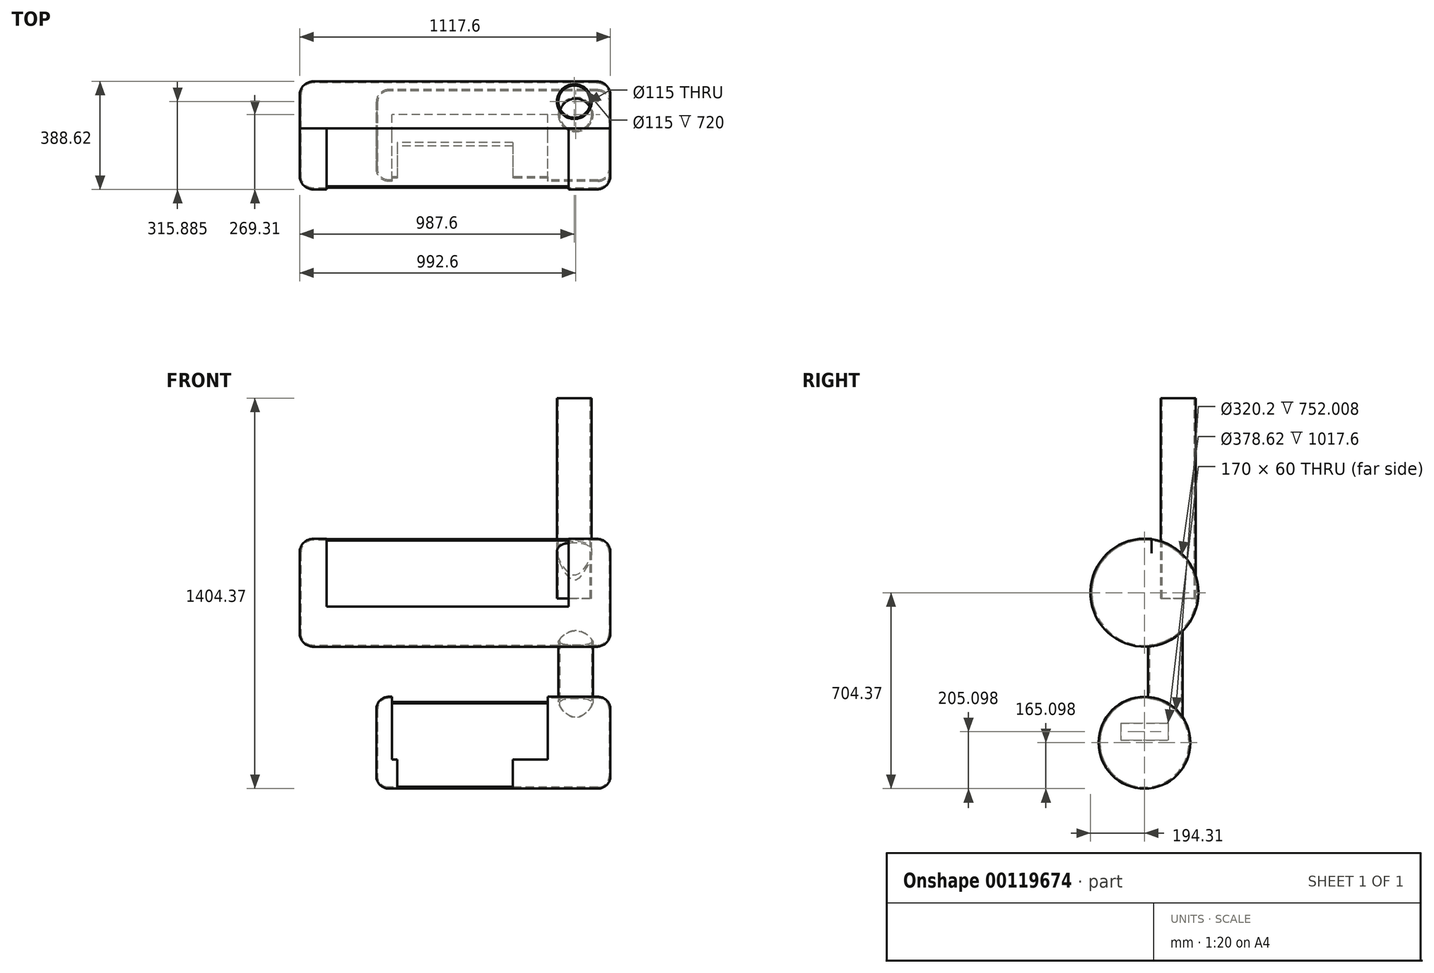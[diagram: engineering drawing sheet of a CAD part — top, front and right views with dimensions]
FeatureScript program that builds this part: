
annotation { "Feature Type Name" : "Feature", "Feature Type Description" : "" }
export const myFeature = defineFeature(function(context is Context, id is Id, definition is map)
    precondition{}
    {
        {
            var Q0;
            Q0=qCreatedBy(makeId("Front.planeOp"),FACE);
            var sketch = newSketch(context, id + "F0", { "sketchPlane" : qUnion([Q0])});
            skLineSegment(sketch, "E0", {"start": v(-542.74, 0) * mm, "end": v(519.1, 0) * mm, "construction": true});
            skLineSegment(sketch, "E1", {"start": v(-558.8, 0) * mm, "end": v(-558.8, 144.3) * mm});
            skLineSegment(sketch, "E2", {"start": v(-508.8, 194.31) * mm, "end": v(508.8, 194.31) * mm});
            skLineSegment(sketch, "E3", {"start": v(558.8, 144.31) * mm, "end": v(558.8, 0) * mm});
            skLineSegment(sketch, "E4", {"start": v(0, 0) * mm, "end": v(0, 194.3) * mm, "construction": true});
            skPoint(sketch, "E5.visualSharp", {"position": v(-558.8, 194.31) * mm});
            skArc(sketch, "E5.filletArc", {"start": v(-508.8, 194.3) * mm, "mid": v(-544.16, 179.67) * mm, "end": v(-558.8, 144.3) * mm});
            skPoint(sketch, "E6.visualSharp", {"position": v(558.8, 194.31) * mm});
            skArc(sketch, "E6.filletArc", {"start": v(558.8, 144.31) * mm, "mid": v(544.16, 179.67) * mm, "end": v(508.8, 194.31) * mm});
            skLineSegment(sketch, "E7.0", {"start": v(553.8, 144.31) * mm, "end": v(553.8, 0) * mm});
            skLineSegment(sketch, "E7.1", {"start": v(-508.8, 189.31) * mm, "end": v(508.8, 189.31) * mm});
            skLineSegment(sketch, "E7.2", {"start": v(-553.8, 0) * mm, "end": v(-553.8, 144.31) * mm});
            skPoint(sketch, "E8.visualSharp", {"position": v(-553.8, 189.31) * mm});
            skArc(sketch, "E8.filletArc", {"start": v(-508.8, 189.31) * mm, "mid": v(-540.62, 176.13) * mm, "end": v(-553.8, 144.31) * mm});
            skPoint(sketch, "E9.visualSharp", {"position": v(553.8, 189.31) * mm});
            skArc(sketch, "E9.filletArc", {"start": v(553.8, 144.31) * mm, "mid": v(540.62, 176.13) * mm, "end": v(508.8, 189.31) * mm});
            skLineSegment(sketch, "E10", {"start": v(-558.8, 0) * mm, "end": v(-553.8, 0) * mm});
            skLineSegment(sketch, "E11", {"start": v(553.8, 0) * mm, "end": v(558.8, 0) * mm});
            skSolve(sketch);
        }
        {
            var Q0;
            Q0 = qSketchRegion(id + "F0", true);
            extrude(context, id + "F1", {"entities" : qUnion([Q0]), "depth" : 25 * mm});
        }
        {
            var Q0;
            Q0=makeQuery(id+"F1.opExtrude","CAP_FACE",FACE,{"disambiguationData":[OSD([sQuery(id+"F0.wireOp",EDGE,"E1"),sQuery(id+"F0.wireOp",EDGE,"E2"),sQuery(id+"F0.wireOp",EDGE,"E3"),sQuery(id+"F0.wireOp",EDGE,"E5.filletArc"),sQuery(id+"F0.wireOp",EDGE,"E6.filletArc"),sQuery(id+"F0.wireOp",EDGE,"E7.0"),sQuery(id+"F0.wireOp",EDGE,"E7.1"),sQuery(id+"F0.wireOp",EDGE,"E7.2"),sQuery(id+"F0.wireOp",EDGE,"E8.filletArc"),sQuery(id+"F0.wireOp",EDGE,"E9.filletArc"),sQuery(id+"F0.wireOp",EDGE,"E10"),sQuery(id+"F0.wireOp",EDGE,"E11")])],"isStart":false});
            var Q1;
            Q1=makeQuery(id+"F1.opExtrude","CAP_EDGE",EDGE,{"disambiguationData":[OSD([sQuery(id+"F0.wireOp",EDGE,"E11")])],"isStart":false});
            revolve(context, id + "F2", {"operationType" : NewBodyOperationType.ADD, "entities" : qUnion([Q0]), "axis" : qUnion([Q1]), "revolveType" : RevolveType.FULL});
        }
        {
            var Q0;
            Q0=qCreatedBy(makeId("Front.planeOp"),FACE);
            cPlane(context, id + "F3", {"entities" : qUnion([Q0]), "cplaneType" : CPlaneType.OFFSET, "offset" : 25 * mm, "width" : 150 * mm, "height" : 150 * mm});
        }
        {
            var Q0;
            Q0=qCreatedBy(makeId("Front.planeOp"),FACE);
            var sketch = newSketch(context, id + "F4", { "sketchPlane" : qUnion([Q0])});
            skLineSegment(sketch, "E12", {"start": v(0, 125.35) * mm, "end": v(0, -125.48) * mm, "construction": true});
            skLineSegment(sketch, "E13.bottom", {"start": v(408.8, 526.72) * mm, "end": v(-461.2, 526.72) * mm});
            skLineSegment(sketch, "E13.top", {"start": v(408.8, -50) * mm, "end": v(-461.2, -50) * mm});
            skLineSegment(sketch, "E13.left", {"start": v(408.8, 526.72) * mm, "end": v(408.8, -50) * mm});
            skLineSegment(sketch, "E13.right", {"start": v(-461.2, 526.72) * mm, "end": v(-461.2, -50) * mm});
            skPoint(sketch, "E13.middle", {"position": v(-26.2, 238.36) * mm});
            skSolve(sketch);
        }
        {
            var Q0;
            Q0 = qSketchRegion(id + "F4", true);
            extrude(context, id + "F5", {"entities" : qUnion([Q0]), "operationType" : NewBodyOperationType.REMOVE, "endBound" : BoundingType.THROUGH_ALL, "depth" : 25 * mm});
        }
        {
            var Q0;
            Q0=qCreatedBy(id+"F3.planeOp",FACE);
            var sketch = newSketch(context, id + "F6", { "sketchPlane" : qUnion([Q0])});
            skLineSegment(sketch, "E14", {"start": v(0, 0) * mm, "end": v(0, -539.27) * mm, "construction": true});
            skLineSegment(sketch, "E15", {"start": v(-471.9, -539.27) * mm, "end": v(471.9, -539.27) * mm, "construction": true});
            skLineSegment(sketch, "E16", {"start": v(-283.2, -539.27) * mm, "end": v(-283.2, -419.17) * mm});
            skLineSegment(sketch, "E17", {"start": v(-238.2, -374.17) * mm, "end": v(513.8, -374.17) * mm});
            skLineSegment(sketch, "E18", {"start": v(558.8, -419.17) * mm, "end": v(558.8, -539.27) * mm});
            skPoint(sketch, "E19.visualSharp", {"position": v(558.8, -374.17) * mm});
            skArc(sketch, "E19.filletArc", {"start": v(558.8, -419.17) * mm, "mid": v(545.62, -387.35) * mm, "end": v(513.8, -374.17) * mm});
            skPoint(sketch, "E20.visualSharp", {"position": v(-283.2, -374.17) * mm});
            skArc(sketch, "E20.filletArc", {"start": v(-238.2, -374.17) * mm, "mid": v(-270.03, -387.35) * mm, "end": v(-283.2, -419.17) * mm});
            skLineSegment(sketch, "E21.0", {"start": v(553.8, -419.17) * mm, "end": v(553.8, -539.27) * mm});
            skLineSegment(sketch, "E21.1", {"start": v(-278.2, -539.27) * mm, "end": v(-278.2, -419.17) * mm});
            skArc(sketch, "E21.2", {"start": v(-238.2, -379.17) * mm, "mid": v(-266.5, -390.89) * mm, "end": v(-278.2, -419.17) * mm});
            skLineSegment(sketch, "E21.3", {"start": v(-238.2, -379.17) * mm, "end": v(513.8, -379.17) * mm});
            skArc(sketch, "E21.4", {"start": v(553.8, -419.17) * mm, "mid": v(542.08, -390.89) * mm, "end": v(513.8, -379.17) * mm});
            skLineSegment(sketch, "E22", {"start": v(-283.2, -539.27) * mm, "end": v(-278.2, -539.27) * mm});
            skLineSegment(sketch, "E23", {"start": v(553.8, -539.27) * mm, "end": v(558.8, -539.27) * mm});
            skSolve(sketch);
        }
        {
            var Q0;
            Q0 = qSketchRegion(id + "F6", true);
            var Q1;
            Q1=sQuery(id+"F6.wireOp",EDGE,"E23");
            revolve(context, id + "F7", {"entities" : qUnion([Q0]), "axis" : qUnion([Q1]), "revolveType" : RevolveType.FULL});
        }
        {
            var Q0;
            Q0=qCreatedBy(makeId("Top.planeOp"),FACE);
            cPlane(context, id + "F8", {"entities" : qUnion([Q0]), "cplaneType" : CPlaneType.OFFSET, "offset" : 300 * mm, "oppositeDirection" : true, "width" : 150 * mm, "height" : 150 * mm});
        }
        {
            var Q0;
            Q0=qCreatedBy(id+"F8.planeOp",FACE);
            var sketch = newSketch(context, id + "F9", { "sketchPlane" : qUnion([Q0])});
            skCircle(sketch, "E24", {"center": v(433.8, 50) * mm, "radius": 62.5 * mm});
            skCircle(sketch, "E25.0", {"center": v(433.8, 50) * mm, "radius": 57.5 * mm});
            skLineSegment(sketch, "E26", {"start": v(0, 0) * mm, "end": v(657.25, 0) * mm, "construction": true});
            skLineSegment(sketch, "E27", {"start": v(433.8, 50) * mm, "end": v(433.8, 0) * mm, "construction": true});
            skSolve(sketch);
        }
        {
            var Q0;
            Q0 = qSketchRegion(id + "F9", true);
            extrude(context, id + "F10", {"entities" : qUnion([Q0]), "operationType" : NewBodyOperationType.ADD, "endBound" : BoundingType.UP_TO_NEXT, "depth" : 25 * mm, "hasSecondDirection" : true, "secondDirectionBound" : SecondDirectionBoundingType.UP_TO_NEXT, "secondDirectionOppositeDirection" : true, "secondDirectionDepth" : 25 * mm});
        }
        {
            var Q0;
            Q0=qCreatedBy(makeId("Top.planeOp"),FACE);
            cPlane(context, id + "F11", {"entities" : qUnion([Q0]), "cplaneType" : CPlaneType.OFFSET, "offset" : 400 * mm, "oppositeDirection" : true, "width" : 150 * mm, "height" : 150 * mm});
        }
        {
            var Q0;
            Q0=qCreatedBy(id+"F11.planeOp",FACE);
            var sketch = newSketch(context, id + "F12", { "sketchPlane" : qUnion([Q0])});
            skLineSegment(sketch, "E28", {"start": v(0, 122.84) * mm, "end": v(0, -200) * mm, "construction": true});
            skLineSegment(sketch, "E29.bottom", {"start": v(-208.2, -50) * mm, "end": v(208.2, -50) * mm});
            skLineSegment(sketch, "E29.top", {"start": v(-208.2, -350) * mm, "end": v(208.2, -350) * mm});
            skLineSegment(sketch, "E29.left", {"start": v(-208.2, -50) * mm, "end": v(-208.2, -350) * mm});
            skLineSegment(sketch, "E29.right", {"start": v(208.2, -50) * mm, "end": v(208.2, -350) * mm});
            skPoint(sketch, "E29.middle", {"position": v(0, -200) * mm});
            skSolve(sketch);
        }
        {
            var Q0;
            Q0 = qSketchRegion(id + "F12", true);
            extrude(context, id + "F13", {"entities" : qUnion([Q0]), "operationType" : NewBodyOperationType.REMOVE, "oppositeDirection" : true, "depth" : 300 * mm, "hasSecondDirection" : true, "secondDirectionOppositeDirection" : false, "secondDirectionDepth" : 5.37 * mm});
        }
        {
            var Q0;
            Q0=qCreatedBy(makeId("Top.planeOp"),FACE);
            var sketch = newSketch(context, id + "F14", { "sketchPlane" : qUnion([Q0])});
            skCircle(sketch, "E30.0", {"center": v(433.8, 50) * mm, "radius": 62.5 * mm, "construction": true});
            skCircle(sketch, "E31", {"center": v(433.8, 50) * mm, "radius": 57.5 * mm});
            skSolve(sketch);
        }
        {
            var Q0;
            Q0 = qSketchRegion(id + "F14", true);
            extrude(context, id + "F15", {"entities" : qUnion([Q0]), "operationType" : NewBodyOperationType.REMOVE, "oppositeDirection" : true, "depth" : 600 * mm});
        }
        {
            var Q0;
            Q0=qCreatedBy(makeId("Front.planeOp"),FACE);
            cPlane(context, id + "F16", {"entities" : qUnion([Q0]), "cplaneType" : CPlaneType.OFFSET, "offset" : 300 * mm, "width" : 150 * mm, "height" : 150 * mm});
        }
        {
            var Q0;
            Q0=qCreatedBy(id+"F16.planeOp",FACE);
            var sketch = newSketch(context, id + "F17", { "sketchPlane" : qUnion([Q0])});
            skLineSegment(sketch, "E32.bottom", {"start": v(-226.2, -350) * mm, "end": v(333.8, -350) * mm});
            skLineSegment(sketch, "E32.top", {"start": v(-226.2, -600) * mm, "end": v(333.8, -600) * mm});
            skLineSegment(sketch, "E32.left", {"start": v(-226.2, -350) * mm, "end": v(-226.2, -600) * mm});
            skLineSegment(sketch, "E32.right", {"start": v(333.8, -350) * mm, "end": v(333.8, -600) * mm});
            skPoint(sketch, "E32.middle", {"position": v(53.8, -475) * mm});
            skSolve(sketch);
        }
        {
            var Q0;
            Q0 = qSketchRegion(id + "F17", true);
            extrude(context, id + "F18", {"entities" : qUnion([Q0]), "operationType" : NewBodyOperationType.REMOVE, "oppositeDirection" : true, "depth" : 350 * mm});
        }
        {
            var Q0;
            Q0=qCreatedBy(makeId("Top.planeOp"),FACE);
            cPlane(context, id + "F19", {"entities" : qUnion([Q0]), "cplaneType" : CPlaneType.OFFSET, "offset" : 700 * mm, "width" : 150 * mm, "height" : 150 * mm});
        }
        {
            var Q0;
            Q0=qCreatedBy(id+"F19.planeOp",FACE);
            var sketch = newSketch(context, id + "F20", { "sketchPlane" : qUnion([Q0])});
            skCircle(sketch, "E33", {"center": v(428.8, 96.57) * mm, "radius": 62.5 * mm});
            skCircle(sketch, "E34.0", {"center": v(428.8, 96.57) * mm, "radius": 57.5 * mm});
            skSolve(sketch);
        }
        {
            var Q0;
            Q0 = qSketchRegion(id + "F20", true);
            extrude(context, id + "F21", {"entities" : qUnion([Q0]), "operationType" : NewBodyOperationType.ADD, "oppositeDirection" : true, "depth" : 720 * mm});
        }
        {
            var Q0;
            Q0=makeQuery(id+"F21.opExtrude","CAP_FACE",FACE,{"disambiguationData":[OSD([sQuery(id+"F20.wireOp",EDGE,"E33"),sQuery(id+"F20.wireOp",EDGE,"E34.0")])],"isStart":true});
            var sketch = newSketch(context, id + "F22", { "sketchPlane" : qUnion([Q0])});
            skCircle(sketch, "E35.0", {"center": v(428.8, 96.57) * mm, "radius": 57.5 * mm});
            skSolve(sketch);
        }
        {
            var Q0;
            Q0 = qSketchRegion(id + "F22", true);
            extrude(context, id + "F23", {"entities" : qUnion([Q0]), "operationType" : NewBodyOperationType.REMOVE, "oppositeDirection" : true, "depth" : 750 * mm});
        }
        {
            var Q0;
            Q0=makeQuery(id+"F7.opRevolve","SWEPT_FACE",FACE,{"disambiguationData":[OSD([sQuery(id+"F6.wireOp",EDGE,"E16")])]});
            var sketch = newSketch(context, id + "F24", { "sketchPlane" : qUnion([Q0])});
            skLineSegment(sketch, "E36", {"start": v(25, -539.27) * mm, "end": v(25, -354.02) * mm, "construction": true});
            skLineSegment(sketch, "E37.bottom", {"start": v(110, -469.27) * mm, "end": v(-60, -469.27) * mm});
            skLineSegment(sketch, "E37.top", {"start": v(110, -529.27) * mm, "end": v(-60, -529.27) * mm});
            skLineSegment(sketch, "E37.left", {"start": v(110, -469.27) * mm, "end": v(110, -529.27) * mm});
            skLineSegment(sketch, "E37.right", {"start": v(-60, -469.27) * mm, "end": v(-60, -529.27) * mm});
            skPoint(sketch, "E37.middle", {"position": v(25, -499.27) * mm});
            skSolve(sketch);
        }
        {
            var Q0;
            Q0 = qSketchRegion(id + "F24", true);
            extrude(context, id + "F25", {"entities" : qUnion([Q0]), "operationType" : NewBodyOperationType.REMOVE, "oppositeDirection" : true, "depth" : 25 * mm});
        }
    });
